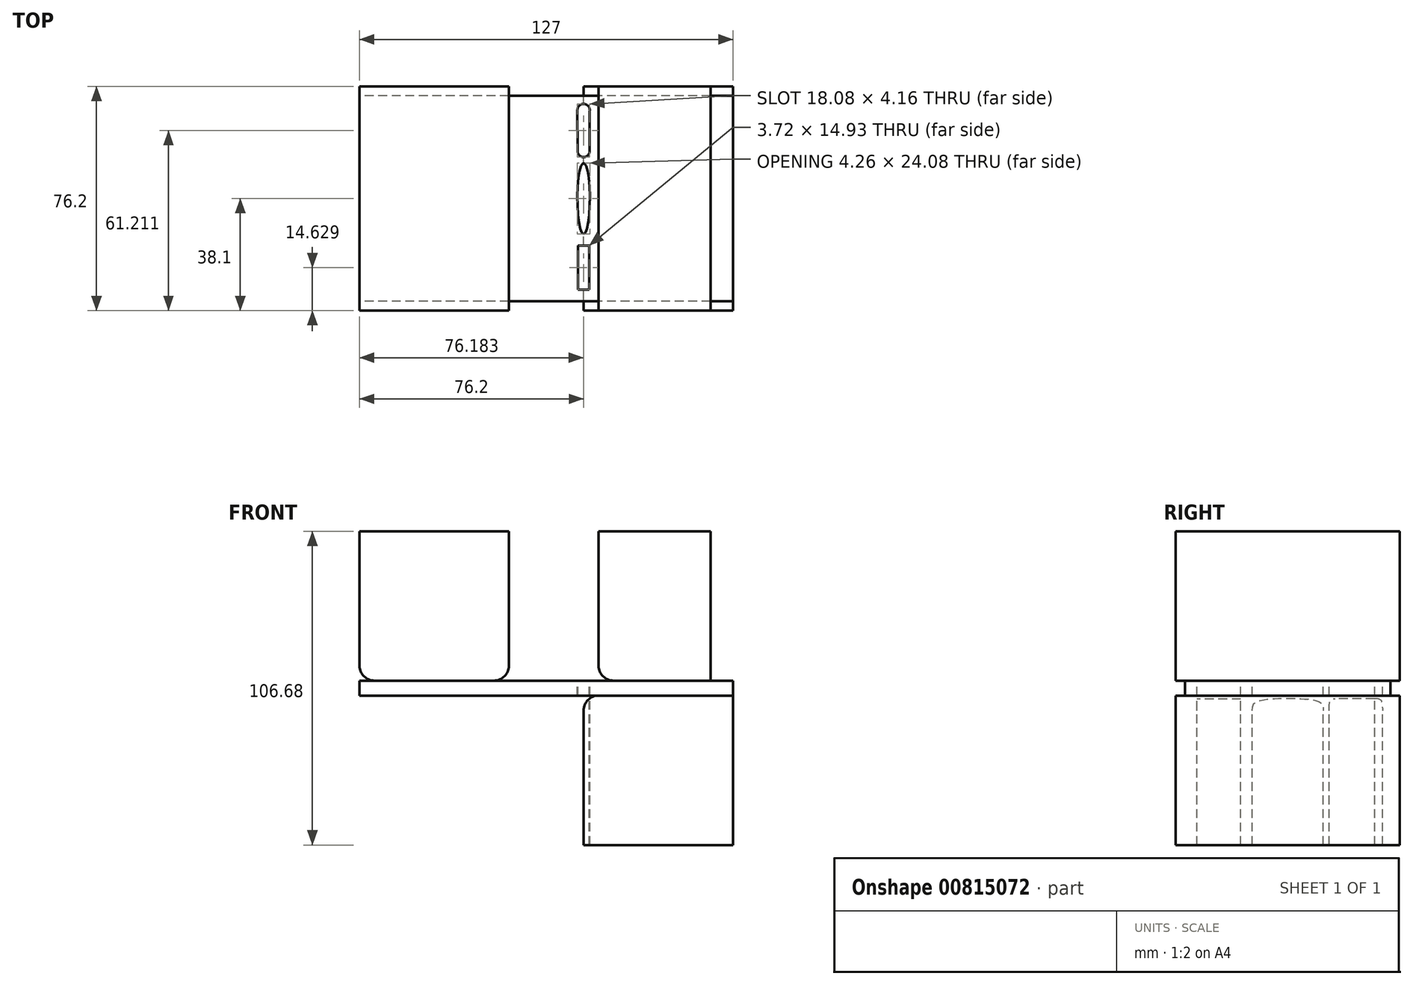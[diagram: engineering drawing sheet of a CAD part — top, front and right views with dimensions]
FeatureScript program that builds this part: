
annotation { "Feature Type Name" : "Feature", "Feature Type Description" : "" }
export const myFeature = defineFeature(function(context is Context, id is Id, definition is map)
    precondition{}
    {
        {
            var Q0;
            Q0=qCreatedBy(makeId("Front.planeOp"),FACE);
            var sketch = newSketch(context, id + "F0", { "sketchPlane" : qUnion([Q0])});
            skLineSegment(sketch, "E0.bottom", {"start": v(0, 0) * mm, "end": v(50.8, 0) * mm});
            skLineSegment(sketch, "E0.top", {"start": v(0, -50.8) * mm, "end": v(50.8, -50.8) * mm});
            skLineSegment(sketch, "E0.left", {"start": v(0, 0) * mm, "end": v(0, -50.8) * mm});
            skLineSegment(sketch, "E0.right", {"start": v(50.8, 0) * mm, "end": v(50.8, -50.8) * mm});
            skLineSegment(sketch, "E1.bottom", {"start": v(50.8, 0) * mm, "end": v(-76.2, 0) * mm});
            skLineSegment(sketch, "E1.top", {"start": v(50.8, 5.08) * mm, "end": v(-76.2, 5.08) * mm});
            skLineSegment(sketch, "E1.left", {"start": v(50.8, 0) * mm, "end": v(50.8, 5.08) * mm});
            skLineSegment(sketch, "E1.right", {"start": v(-76.2, 0) * mm, "end": v(-76.2, 5.08) * mm});
            skLineSegment(sketch, "E2", {"start": v(0, 5.08) * mm, "end": v(5.08, 5.08) * mm});
            skLineSegment(sketch, "E3.bottom", {"start": v(5.08, 5.08) * mm, "end": v(43.18, 5.08) * mm});
            skLineSegment(sketch, "E3.top", {"start": v(5.08, 55.88) * mm, "end": v(43.18, 55.88) * mm});
            skLineSegment(sketch, "E3.left", {"start": v(5.08, 5.08) * mm, "end": v(5.08, 55.88) * mm});
            skLineSegment(sketch, "E3.right", {"start": v(43.18, 5.08) * mm, "end": v(43.18, 55.88) * mm});
            skLineSegment(sketch, "E4.bottom", {"start": v(-76.2, 5.08) * mm, "end": v(-25.4, 5.08) * mm});
            skLineSegment(sketch, "E4.top", {"start": v(-76.2, 55.88) * mm, "end": v(-25.4, 55.88) * mm});
            skLineSegment(sketch, "E4.left", {"start": v(-76.2, 5.08) * mm, "end": v(-76.2, 55.88) * mm});
            skLineSegment(sketch, "E4.right", {"start": v(-25.4, 5.08) * mm, "end": v(-25.4, 55.88) * mm});
            skSolve(sketch);
        }
        {
            var Q0;
            Q0=makeQuery(id+"F0.imprint","IMPRINT",FACE,{"disambiguationData":[TD([[makeQuery(id+"F0.imprint","IMPRINT",EDGE,{"derivedFrom":sQuery(id+"F0.wireOp",EDGE,"E0.bottom")}),-1.0]])]});
            var Q1;
            Q1=makeQuery(id+"F0.imprint","IMPRINT",FACE,{"disambiguationData":[TD([[makeQuery(id+"F0.imprint","IMPRINT",EDGE,{"derivedFrom":sQuery(id+"F0.wireOp",EDGE,"E4.top")}),-1.0]])]});
            extrude(context, id + "F1", {"entities" : qUnion([Q0, Q1]), "endBound" : BoundingType.SYMMETRIC, "depth" : 76.2 * mm, "offsetDistance" : 25.4 * mm});
        }
        {
            var Q0;
            Q0=makeQuery(id+"F0.imprint","IMPRINT",FACE,{"disambiguationData":[TD([[makeQuery(id+"F0.imprint","IMPRINT",EDGE,{"derivedFrom":sQuery(id+"F0.wireOp",EDGE,"E3.top")}),-1.0]])]});
            extrude(context, id + "F2", {"entities" : qUnion([Q0]), "endBound" : BoundingType.SYMMETRIC, "depth" : 76.2 * mm, "offsetDistance" : 25.4 * mm});
        }
        {
            var Q0;
            Q0=makeQuery(id+"F0.imprint","IMPRINT",FACE,{"disambiguationData":[TD([[makeQuery(id+"F0.imprint","IMPRINT",EDGE,{"derivedFrom":sQuery(id+"F0.wireOp",EDGE,"E0.bottom")}),1.0]])]});
            extrude(context, id + "F3", {"entities" : qUnion([Q0]), "endBound" : BoundingType.SYMMETRIC, "depth" : 69.85 * mm, "offsetDistance" : 25.4 * mm});
        }
        {
            var Q0;
            Q0=makeQuery(id+"F1.opExtrude","SWEPT_EDGE",EDGE,{"disambiguationData":[OSD([sQuery(id+"F0.wireOp",EDGE,"E1.top"),sQuery(id+"F0.wireOp",EDGE,"E1.right"),sQuery(id+"F0.wireOp",EDGE,"E4.left")])]});
            var Q1;
            Q1=makeQuery(id+"F1.opExtrude","SWEPT_EDGE",EDGE,{"disambiguationData":[OSD([sQuery(id+"F0.wireOp",EDGE,"E1.top"),sQuery(id+"F0.wireOp",EDGE,"E4.right")])]});
            var Q2;
            Q2=makeQuery(id+"F2.opExtrude","SWEPT_EDGE",EDGE,{"disambiguationData":[OSD([sQuery(id+"F0.wireOp",EDGE,"E1.top"),sQuery(id+"F0.wireOp",EDGE,"E3.left")])]});
            var Q3;
            Q3=makeQuery(id+"F1.opExtrude","SWEPT_EDGE",EDGE,{"disambiguationData":[OSD([sQuery(id+"F0.wireOp",EDGE,"E0.bottom"),sQuery(id+"F0.wireOp",EDGE,"E0.left"),sQuery(id+"F0.wireOp",EDGE,"E1.bottom")])]});
            fillet(context, id + "F4", {"entities" : qUnion([Q0, Q1, Q2, Q3]), "radius" : 5.08 * mm, "tangentPropagation" : true, "allowEdgeOverflow" : false});
        }
        {
            var Q0;
            Q0=makeQuery(id+"F3.opExtrude","SWEPT_FACE",FACE,{"disambiguationData":[OSD([sQuery(id+"F0.wireOp",EDGE,"E1.top")])]});
            var sketch = newSketch(context, id + "F5", { "sketchPlane" : qUnion([Q0])});
            skLineSegment(sketch, "E5", {"start": v(0, 0) * mm, "end": v(0, 34.93) * mm});
            skLineSegment(sketch, "E6", {"start": v(0, 34.93) * mm, "end": v(0, -34.93) * mm});
            skLineSegment(sketch, "E7.bottom", {"start": v(1.86, -16) * mm, "end": v(-1.86, -16) * mm});
            skLineSegment(sketch, "E7.top", {"start": v(1.86, -30.94) * mm, "end": v(-1.86, -30.94) * mm});
            skLineSegment(sketch, "E7.left", {"start": v(1.86, -16) * mm, "end": v(1.86, -30.94) * mm});
            skLineSegment(sketch, "E7.right", {"start": v(-1.86, -16) * mm, "end": v(-1.86, -30.94) * mm});
            skPoint(sketch, "E7.middle", {"position": v(0, -23.47) * mm});
            skEllipse(sketch, "E8", {"center": v(0, 0) * mm, "majorRadius": 12.04 * mm, "minorRadius": 2.13 * mm, "majorAxis": v(0, -1)});
            skCircle(sketch, "E9", {"center": v(0, 16.1) * mm, "radius": 2.04 * mm});
            skCircle(sketch, "E10", {"center": v(0, 30.07) * mm, "radius": 2.1 * mm});
            skLineSegment(sketch, "E11", {"start": v(-2.1, 30.07) * mm, "end": v(-2.04, 16.1) * mm});
            skLineSegment(sketch, "E12", {"start": v(2.04, 16.1) * mm, "end": v(2.04, 30.07) * mm});
            skSolve(sketch);
        }
        {
            var Q0;
            Q0 = qSketchRegion(id + "F5", true);
            extrude(context, id + "F6", {"entities" : qUnion([Q0]), "operationType" : NewBodyOperationType.REMOVE, "endBound" : BoundingType.THROUGH_ALL, "oppositeDirection" : true, "depth" : 25.4 * mm, "offsetDistance" : 25.4 * mm});
        }
    });
